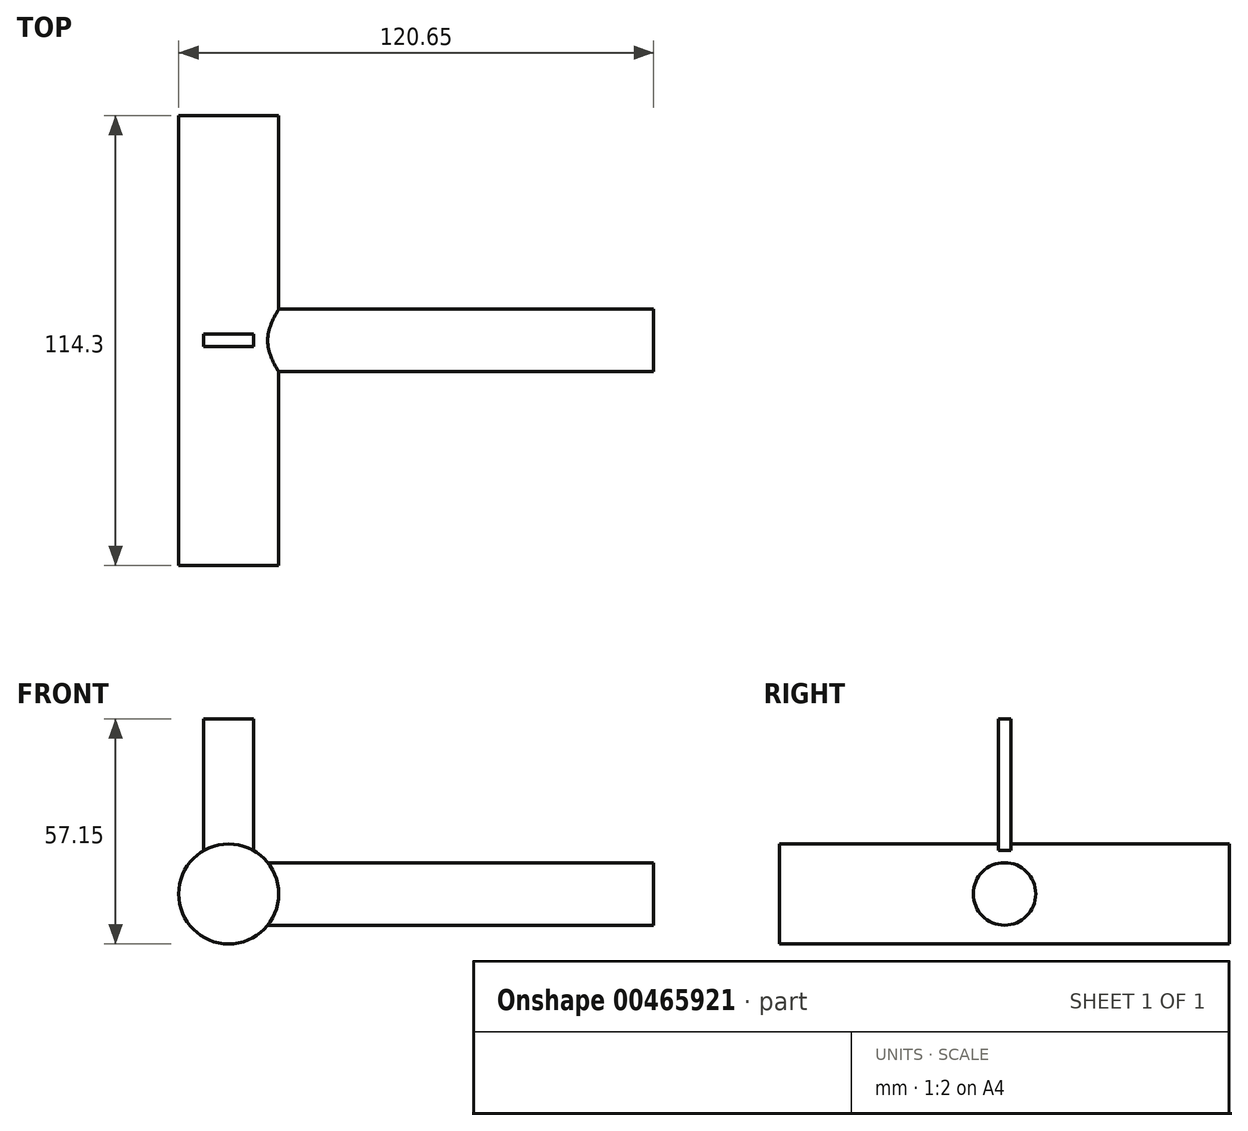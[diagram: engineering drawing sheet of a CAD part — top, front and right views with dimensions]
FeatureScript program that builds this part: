
annotation { "Feature Type Name" : "Feature", "Feature Type Description" : "" }
export const myFeature = defineFeature(function(context is Context, id is Id, definition is map)
    precondition{}
    {
        {
            var Q0;
            Q0=qCreatedBy(makeId("Front.planeOp"),FACE);
            var sketch = newSketch(context, id + "F0", { "sketchPlane" : qUnion([Q0])});
            skCircle(sketch, "E0", {"center": v(0, 0) * mm, "radius": 12.7 * mm});
            skSolve(sketch);
        }
        {
            var Q0;
            Q0=qCreatedBy(makeId("Right.planeOp"),FACE);
            var sketch = newSketch(context, id + "F1", { "sketchPlane" : qUnion([Q0])});
            skCircle(sketch, "E1", {"center": v(0, 0) * mm, "radius": 7.94 * mm});
            skSolve(sketch);
        }
        {
            var Q0;
            Q0=makeQuery(id+"F1.imprint","IMPRINT",FACE,{"disambiguationData":[TD([[makeQuery(id+"F1.imprint","IMPRINT",EDGE,{"derivedFrom":sQuery(id+"F1.wireOp",EDGE,"E1")}),1.0]])]});
            extrude(context, id + "F2", {"entities" : qUnion([Q0]), "depth" : 107.95 * mm});
        }
        {
            var Q0;
            Q0=makeQuery(id+"F0.imprint","IMPRINT",FACE,{"disambiguationData":[TD([[makeQuery(id+"F0.imprint","IMPRINT",EDGE,{"derivedFrom":sQuery(id+"F0.wireOp",EDGE,"E0")}),1.0]])]});
            extrude(context, id + "F3", {"entities" : qUnion([Q0]), "operationType" : NewBodyOperationType.ADD, "endBound" : BoundingType.SYMMETRIC, "depth" : 114.3 * mm});
        }
        {
            var Q0;
            Q0=qCreatedBy(makeId("Front.planeOp"),FACE);
            var sketch = newSketch(context, id + "F4", { "sketchPlane" : qUnion([Q0])});
            skLineSegment(sketch, "E2", {"start": v(0, 0) * mm, "end": v(0, 12.7) * mm});
            skLineSegment(sketch, "E3", {"start": v(0, 12.7) * mm, "end": v(0, 6.35) * mm});
            skLineSegment(sketch, "E4", {"start": v(0, 6.35) * mm, "end": v(6.35, 6.35) * mm});
            skLineSegment(sketch, "E5", {"start": v(6.35, 6.35) * mm, "end": v(-6.35, 6.35) * mm});
            skLineSegment(sketch, "E6", {"start": v(-6.35, 6.35) * mm, "end": v(-6.35, 44.45) * mm});
            skLineSegment(sketch, "E7", {"start": v(-6.35, 44.45) * mm, "end": v(6.35, 44.45) * mm});
            skLineSegment(sketch, "E8", {"start": v(6.35, 44.45) * mm, "end": v(6.35, 6.35) * mm});
            skSolve(sketch);
        }
        {
            var Q0;
            {var subQ0=sQuery(id+"F4.wireOp",EDGE,"E6");Q0=makeQuery(id+"F4.imprint","IMPRINT",FACE,{"disambiguationData":[TD([[makeQuery(id+"F4.imprint","IMPRINT",EDGE,{"derivedFrom":subQ0}),-1.0]])]});}
            extrude(context, id + "F5", {"entities" : qUnion([Q0]), "operationType" : NewBodyOperationType.ADD, "endBound" : BoundingType.SYMMETRIC, "depth" : 3.17 * mm});
        }
    });
